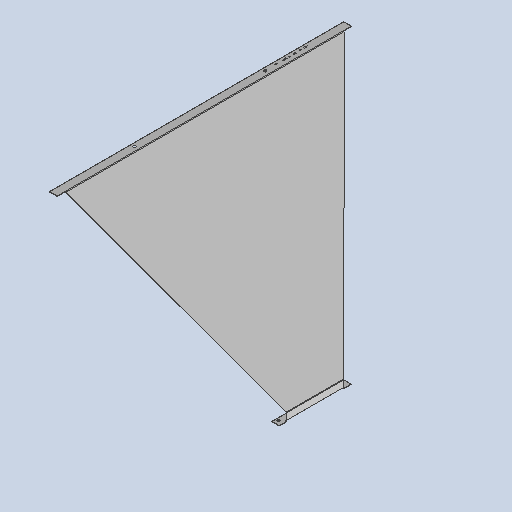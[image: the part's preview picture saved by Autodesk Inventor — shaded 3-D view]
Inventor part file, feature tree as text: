
AUTODESK INVENTOR PART (.ipt)
format: ipt  version: 2025 (Build 290162010, 162A)  size: 437,248 bytes
history: native  units: mm
features: sheet_metal_op x9, sketch x8, other x8, extrude x2, projected_geometry x2, mirror x1, pattern_linear x1
ambient origin geometry x8: Origin, YZ Plane, XZ Plane, XY Plane, X Axis, Y Axis, Z Axis, Center Point
bodies: Solid1 (feature_tree)
feature tree (31):
  sheet_metal_op  "Contour Flange1"
  extrude  "Extrusion10"  Depth=3.0mm
  mirror  "Mirror1"
  sketch  "Sketch16"  dims[d10=5.0mm d11=1700.0mm]
  extrude  "Extrusion11"  Depth=6.0mm
  other  "Mark3"
  other  "A-Side Definition"
  sheet_metal_op  "Flange3"
  sheet_metal_op  "Flange4"
  pattern_linear  "Rectangular Pattern1"  Count1=170  [1 undecoded]
  sketch  "Sketch1"  dims[d6=3.0mm d7=3.0mm]
  other  "Plate1"
  sheet_metal_op  "Bend1"
  sheet_metal_op  "Corner1"
  sketch  "Sketch15"  dims[d8=1.5mm d9=6.0mm]
  projected_geometry  "Projected Loop9"
  sketch  "Sketch17"  dims[d12=5.0mm]
  projected_geometry  "Projected Loop10"
  sketch  "Sketch18"  dims[d13=4.0mm]
  other  "Plate4"
  sheet_metal_op  "Bend4"
  sheet_metal_op  "Corner4"
  sketch  "Sketch19"  dims[d14=12.0mm]
  other  "Plate5"
  sheet_metal_op  "Bend5"
  sheet_metal_op  "Corner5"
  sketch  "Sketch20"  dims[d15=3.0mm]
  sketch  "Sketch21"  dims[d16=5.0mm d65=0.0mm d66=1170.0mm d68=50.0mm d70=5.0mm d79=875.499815mm d84=120.0deg d85=50.0mm d86=0.0mm d87=11.059943mm d88=2.0mm d89=0.0mm d90=0.0mm d91=200.0mm d92=350.0mm d93=3.0mm d94=1.5mm d95=6.0mm d96=5.0mm d97=50.0mm d98=30.0deg d99=5.0mm d100=12.0mm d101=3.0mm d102=5.0mm d103=3.0mm d104=1.5mm d105=6.0mm d106=5.0mm d107=45.0mm d108=90.0deg d109=5.0mm d110=12.0mm d111=3.0mm d112=5.0mm d113=14.0mm d114=15.0mm d115=3.0mm d116=0.0mm d117=30.0mm d119=195.0mm d120=-45.0mm d121=-45.0mm d122=16.0mm d123=800.0mm d124=20.0mm d125=3.0mm d126=0.0mm]
  other  "Cut1"
  other  "Cut2"
  other  "Definition1"
note: 1 required parameter value undecoded (feature->parameter linkage not recoverable at this tier; creation-order binding heuristic only, values carry confidence <= 0.55)
